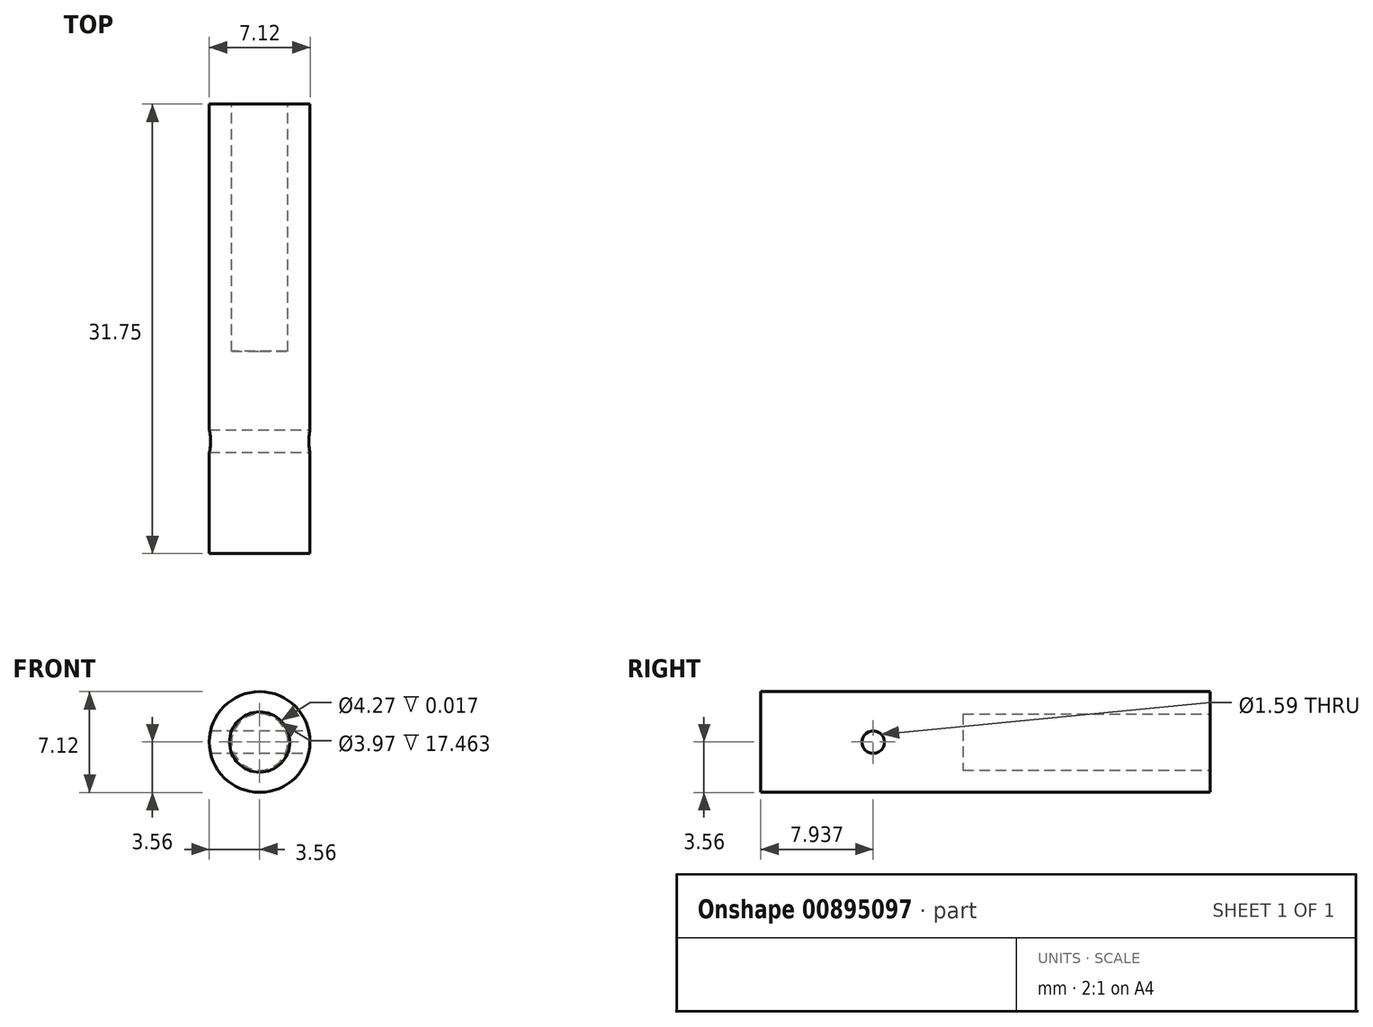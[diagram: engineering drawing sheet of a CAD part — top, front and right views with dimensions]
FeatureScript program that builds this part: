
annotation { "Feature Type Name" : "Feature", "Feature Type Description" : "" }
export const myFeature = defineFeature(function(context is Context, id is Id, definition is map)
    precondition{}
    {
        {
            var Q0;
            Q0=qCreatedBy(makeId("Front.planeOp"),FACE);
            var sketch = newSketch(context, id + "F0", { "sketchPlane" : qUnion([Q0])});
            skCircle(sketch, "E0", {"center": v(0, 0) * mm, "radius": 3.56 * mm});
            skSolve(sketch);
        }
        {
            var Q0;
            Q0 = qSketchRegion(id + "F0", true);
            extrude(context, id + "F1", {"entities" : qUnion([Q0]), "flatOperationType" : FlatOperationType.REMOVE, "depth" : 25.4 * mm, "offsetDistance" : 25.4 * mm, "domain" : OperationDomain.MODEL, "symmetric" : true});
        }
        {
            var Q0;
            Q0=makeQuery(id+"F1.opExtrude","CAP_FACE",FACE,{"disambiguationData":[OSD([sQuery(id+"F0.wireOp",EDGE,"E0")])],"isStart":false});
            var sketch = newSketch(context, id + "F2", { "sketchPlane" : qUnion([Q0])});
            skCircle(sketch, "E1", {"center": v(0, 0) * mm, "radius": 2.13 * mm});
            skSolve(sketch);
        }
        {
            var Q0;
            Q0=makeQuery(id+"F1.opExtrude","CAP_FACE",FACE,{"disambiguationData":[OSD([sQuery(id+"F0.wireOp",EDGE,"E0")])],"isStart":true});
            var sketch = newSketch(context, id + "F3", { "sketchPlane" : qUnion([Q0])});
            skCircle(sketch, "E2", {"center": v(0, 0) * mm, "radius": 1.98 * mm});
            skSolve(sketch);
        }
        {
            var Q0;
            Q0 = qSketchRegion(id + "F2", true);
            var Q1;
            Q1 = qSketchRegion(id + "F3", true);
            extrude(context, id + "F4", {"entities" : qUnion([Q0, Q1]), "operationType" : NewBodyOperationType.REMOVE, "flatOperationType" : FlatOperationType.REMOVE, "oppositeDirection" : true, "depth" : 7 / 406.4 * mm, "offsetDistance" : 25.4 * mm, "domain" : OperationDomain.MODEL});
        }
        {
            var Q0;
            Q0 = qSketchRegion(id + "F3", true);
            var Q1;
            Q1 = qConstructionFilter(qBodyType(qCreatedBy(id + "F3" ,EDGE), BodyType.WIRE), ConstructionObject.NO);
            extrude(context, id + "F5", {"entities" : qUnion([Q0]), "operationType" : NewBodyOperationType.REMOVE, "flatOperationType" : FlatOperationType.REMOVE, "surfaceEntities" : qUnion([Q1]), "oppositeDirection" : true, "depth" : 11.1 * mm, "offsetDistance" : 25.4 * mm, "domain" : OperationDomain.MODEL});
        }
        {
            var Q0;
            Q0=qCreatedBy(makeId("Right.planeOp"),FACE);
            var sketch = newSketch(context, id + "F6", { "sketchPlane" : qUnion([Q0])});
            skCircle(sketch, "E3", {"center": v(-4.76, 0) * mm, "radius": 0.8 * mm});
            skSolve(sketch);
        }
        {
            var Q0;
            Q0 = qSketchRegion(id + "F6", true);
            extrude(context, id + "F7", {"entities" : qUnion([Q0]), "operationType" : NewBodyOperationType.REMOVE, "flatOperationType" : FlatOperationType.REMOVE, "endBound" : BoundingType.THROUGH_ALL, "oppositeDirection" : true, "depth" : 8.28 * mm, "offsetDistance" : 25.4 * mm, "hasSecondDirection" : true, "secondDirectionBound" : BoundingType.THROUGH_ALL, "secondDirectionOppositeDirection" : false, "secondDirectionDepth" : 25.4 * mm, "domain" : OperationDomain.MODEL});
        }
        {
            var Q0;
            Q0=makeQuery(id+"F1.opExtrude","CAP_FACE",FACE,{"disambiguationData":[OSD([sQuery(id+"F0.wireOp",EDGE,"E0")])],"isStart":true});
            extrude(context, id + "F8", {"entities" : qUnion([Q0]), "operationType" : NewBodyOperationType.ADD, "flatOperationType" : FlatOperationType.REMOVE, "depth" : 6.35 * mm, "offsetDistance" : 25.4 * mm, "domain" : OperationDomain.MODEL});
        }
    });
